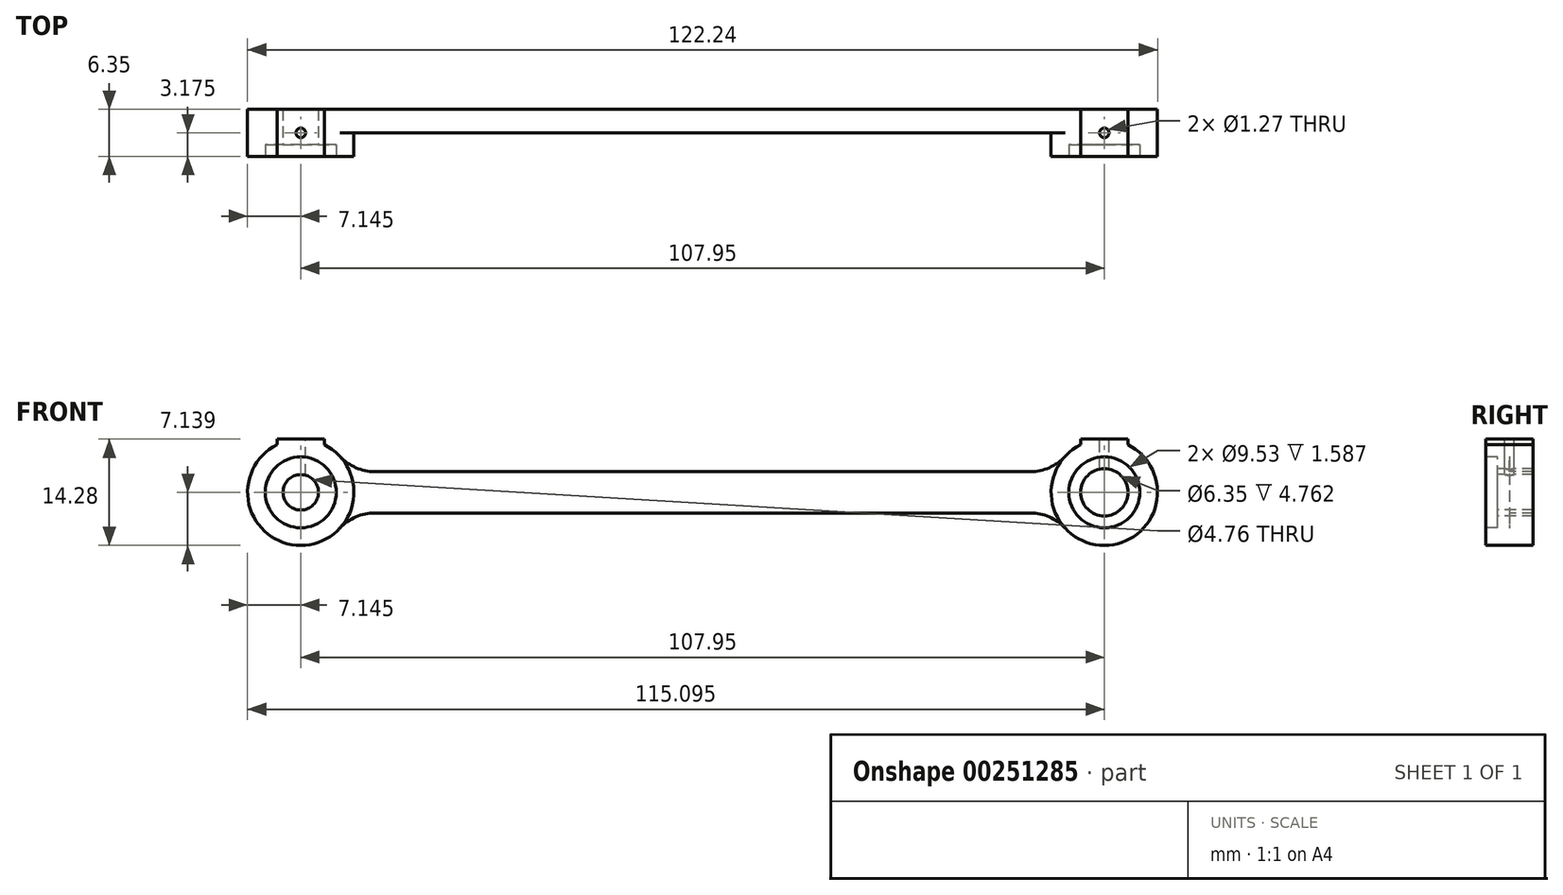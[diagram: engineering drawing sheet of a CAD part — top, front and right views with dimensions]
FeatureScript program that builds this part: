
annotation { "Feature Type Name" : "Feature", "Feature Type Description" : "" }
export const myFeature = defineFeature(function(context is Context, id is Id, definition is map)
    precondition{}
    {
        {
            var Q0;
            Q0=qCreatedBy(makeId("Front.planeOp"),FACE);
            var sketch = newSketch(context, id + "F0", { "sketchPlane" : qUnion([Q0])});
            skLineSegment(sketch, "E0", {"start": v(3.78, 14.91) * mm, "end": v(111.73, 14.91) * mm});
            skLineSegment(sketch, "E1", {"start": v(111.73, 14.91) * mm, "end": v(111.73, 20.47) * mm});
            skLineSegment(sketch, "E2", {"start": v(111.73, 20.47) * mm, "end": v(3.78, 20.47) * mm});
            skLineSegment(sketch, "E3", {"start": v(3.78, 20.47) * mm, "end": v(3.78, 14.91) * mm});
            skSolve(sketch);
        }
        {
            var Q0;
            Q0 = qSketchRegion(id + "F0", true);
            extrude(context, id + "F1", {"entities" : qUnion([Q0]), "depth" : 3.17 * mm});
        }
        {
            var Q0;
            Q0=makeQuery(id+"F1.opExtrude","CAP_FACE",FACE,{"disambiguationData":[OSD([sQuery(id+"F0.wireOp",EDGE,"E0"),sQuery(id+"F0.wireOp",EDGE,"E1"),sQuery(id+"F0.wireOp",EDGE,"E2"),sQuery(id+"F0.wireOp",EDGE,"E3")])],"isStart":false});
            var sketch = newSketch(context, id + "F2", { "sketchPlane" : qUnion([Q0])});
            skCircle(sketch, "E4", {"center": v(3.78, 17.69) * mm, "radius": 7.14 * mm});
            skSolve(sketch);
        }
        {
            var Q0;
            Q0 = qSketchRegion(id + "F2", true);
            extrude(context, id + "F3", {"entities" : qUnion([Q0]), "operationType" : NewBodyOperationType.ADD, "oppositeDirection" : true, "depth" : 3.17 * mm});
        }
        {
            var Q0;
            Q0=makeQuery(id+"F3.boolean.opBoolean","MERGE",FACE,{"derivedFrom":[makeQuery(id+"F1.opExtrude","CAP_FACE",FACE,{"disambiguationData":[OSD([sQuery(id+"F0.wireOp",EDGE,"E0"),sQuery(id+"F0.wireOp",EDGE,"E1"),sQuery(id+"F0.wireOp",EDGE,"E2"),sQuery(id+"F0.wireOp",EDGE,"E3")])],"isStart":false}),makeQuery(id+"F3.opExtrude","CAP_FACE",FACE,{"disambiguationData":[OSD([sQuery(id+"F2.wireOp",EDGE,"E4")])],"isStart":true})]});
            var sketch = newSketch(context, id + "F4", { "sketchPlane" : qUnion([Q0])});
            skCircle(sketch, "E5", {"center": v(3.78, 17.69) * mm, "radius": 7.14 * mm});
            skSolve(sketch);
        }
        {
            var Q0;
            Q0 = qSketchRegion(id + "F4", true);
            extrude(context, id + "F5", {"entities" : qUnion([Q0]), "operationType" : NewBodyOperationType.ADD, "depth" : 3.17 * mm});
        }
        {
            var Q0;
            Q0=makeQuery(id+"F5.opExtrude","CAP_FACE",FACE,{"disambiguationData":[OSD([sQuery(id+"F4.wireOp",EDGE,"E5")])],"isStart":false});
            var sketch = newSketch(context, id + "F6", { "sketchPlane" : qUnion([Q0])});
            skCircle(sketch, "E6", {"center": v(3.78, 17.69) * mm, "radius": 2.38 * mm});
            skSolve(sketch);
        }
        {
            var Q0;
            Q0 = qSketchRegion(id + "F6", true);
            extrude(context, id + "F7", {"entities" : qUnion([Q0]), "operationType" : NewBodyOperationType.REMOVE, "oppositeDirection" : true, "depth" : 25.4 * mm});
        }
        {
            var Q0;
            Q0=makeQuery(id+"F5.opExtrude","CAP_FACE",FACE,{"disambiguationData":[OSD([sQuery(id+"F4.wireOp",EDGE,"E5")])],"isStart":false});
            var sketch = newSketch(context, id + "F8", { "sketchPlane" : qUnion([Q0])});
            skCircle(sketch, "E7", {"center": v(3.78, 17.69) * mm, "radius": 4.76 * mm});
            skSolve(sketch);
        }
        {
            var Q0;
            Q0 = qSketchRegion(id + "F8", true);
            extrude(context, id + "F9", {"entities" : qUnion([Q0]), "operationType" : NewBodyOperationType.REMOVE, "oppositeDirection" : true, "depth" : 1.59 * mm});
        }
        {
            var Q0;
            Q0=makeQuery(id+"F5.opExtrude","CAP_FACE",FACE,{"disambiguationData":[OSD([sQuery(id+"F4.wireOp",EDGE,"E5")])],"isStart":false});
            var sketch = newSketch(context, id + "F10", { "sketchPlane" : qUnion([Q0])});
            skLineSegment(sketch, "E8", {"start": v(-3.24, 24.83) * mm, "end": v(11.05, 24.83) * mm});
            skLineSegment(sketch, "E9", {"start": v(0.6, 24.83) * mm, "end": v(0.6, 24.09) * mm});
            skLineSegment(sketch, "E10", {"start": v(3.78, 17.69) * mm, "end": v(3.78, 24.83) * mm});
            skLineSegment(sketch, "E11", {"start": v(6.96, 24.83) * mm, "end": v(6.96, 24.09) * mm});
            skArc(sketch, "E12", {"start": v(0.6, 24.09) * mm, "mid": v(3.78, 24.83) * mm, "end": v(6.96, 24.09) * mm});
            skSolve(sketch);
        }
        {
            var Q0;
            Q0 = qSketchRegion(id + "F10", true);
            extrude(context, id + "F11", {"entities" : qUnion([Q0]), "oppositeDirection" : true, "depth" : 6.35 * mm});
        }
        {
            var Q0;
            {var subQ0=sQuery(id+"F10.wireOp",EDGE,"E8");Q0=makeQuery(id+"F11.opExtrude","SWEPT_FACE",FACE,{"disambiguationData":[OSD([subQ0]),TDD([makeQuery(id+"F10.imprint","IMPRINT",EDGE,{"disambiguationData":[TD([[makeQuery(id+"F10.imprint","INTERSECT",VERTEX,{"derivedFrom":[subQ0,sQuery(id+"F10.wireOp",EDGE,"E9")]}),-1.0]])],"derivedFrom":subQ0})])]});}
            var sketch = newSketch(context, id + "F12", { "sketchPlane" : qUnion([Q0])});
            skCircle(sketch, "E13", {"center": v(3.78, -3.17) * mm, "radius": 0.64 * mm});
            skSolve(sketch);
        }
        {
            var Q0;
            Q0=makeQuery(id+"F1.opExtrude","SWEPT_BODY",BODY,{"disambiguationData":[OSD([sQuery(id+"F0.wireOp",EDGE,"E0"),sQuery(id+"F0.wireOp",EDGE,"E1"),sQuery(id+"F0.wireOp",EDGE,"E2"),sQuery(id+"F0.wireOp",EDGE,"E3")])]});
            var Q1;
            Q1=makeQuery(id+"F11.opExtrude","SWEPT_BODY",BODY,{"disambiguationData":[OSD([sQuery(id+"F10.wireOp",EDGE,"E8"),sQuery(id+"F10.wireOp",EDGE,"E9"),sQuery(id+"F10.wireOp",EDGE,"E12")])]});
            var Q2;
            Q2=makeQuery(id+"F11.opExtrude","SWEPT_BODY",BODY,{"disambiguationData":[OSD([sQuery(id+"F10.wireOp",EDGE,"E8"),sQuery(id+"F10.wireOp",EDGE,"E11"),sQuery(id+"F10.wireOp",EDGE,"E12")])]});
            booleanBodies(context, id + "F13", {"operationType" : BooleanOperationType.UNION, "tools" : qUnion([Q0, Q1, Q2])});
        }
        {
            var Q0;
            {var subQ0=sQuery(id+"F12.wireOp",EDGE,"E13");var subQ1=sQuery(id+"F10.wireOp",EDGE,"E12");var subQ2=sQuery(id+"F10.wireOp",EDGE,"E8");var subQ3=makeQuery(id+"F11.opExtrude","SWEPT_EDGE",EDGE,{"disambiguationData":[OSD([subQ2,subQ1]),ownerDisambiguation([makeQuery(id+"F11.opExtrude","SWEPT_BODY",BODY,{"disambiguationData":[OSD([subQ2,sQuery(id+"F10.wireOp",EDGE,"E9"),subQ1])]})])]});var subQ4=makeQuery(id+"F12.imprint","INTERSECT",VERTEX,{"disambiguationData":[OD(0.0)],"derivedFrom":[subQ3,subQ0]});Q0=makeQuery(id+"F12.imprint","IMPRINT",FACE,{"disambiguationData":[TD([[makeQuery(id+"F12.imprint","IMPRINT",EDGE,{"disambiguationData":[TD([[subQ4,1.0]])],"derivedFrom":subQ0}),1.0]])]});}
            var Q1;
            {var subQ0=sQuery(id+"F12.wireOp",EDGE,"E13");var subQ1=sQuery(id+"F10.wireOp",EDGE,"E12");var subQ2=sQuery(id+"F10.wireOp",EDGE,"E8");var subQ3=makeQuery(id+"F11.opExtrude","SWEPT_EDGE",EDGE,{"disambiguationData":[OSD([subQ2,subQ1]),ownerDisambiguation([makeQuery(id+"F11.opExtrude","SWEPT_BODY",BODY,{"disambiguationData":[OSD([subQ2,sQuery(id+"F10.wireOp",EDGE,"E9"),subQ1])]})])]});var subQ4=makeQuery(id+"F12.imprint","INTERSECT",VERTEX,{"disambiguationData":[OD(0.0)],"derivedFrom":[subQ3,subQ0]});Q1=makeQuery(id+"F12.imprint","IMPRINT",FACE,{"disambiguationData":[TD([[makeQuery(id+"F12.imprint","IMPRINT",EDGE,{"disambiguationData":[TD([[subQ4,-1.0]])],"derivedFrom":subQ0}),1.0]])]});}
            extrude(context, id + "F14", {"entities" : qUnion([Q0, Q1]), "operationType" : NewBodyOperationType.REMOVE, "oppositeDirection" : true, "depth" : 6.35 * mm});
        }
        {
            var Q0;
            Q0=makeQuery(id+"F3.boolean.opBoolean","MERGE",FACE,{"derivedFrom":[makeQuery(id+"F1.opExtrude","CAP_FACE",FACE,{"disambiguationData":[OSD([sQuery(id+"F0.wireOp",EDGE,"E0"),sQuery(id+"F0.wireOp",EDGE,"E1"),sQuery(id+"F0.wireOp",EDGE,"E2"),sQuery(id+"F0.wireOp",EDGE,"E3")])],"isStart":false}),makeQuery(id+"F3.opExtrude","CAP_FACE",FACE,{"disambiguationData":[OSD([sQuery(id+"F2.wireOp",EDGE,"E4")])],"isStart":true})]});
            var sketch = newSketch(context, id + "F15", { "sketchPlane" : qUnion([Q0])});
            skCircle(sketch, "E14", {"center": v(111.73, 17.69) * mm, "radius": 7.14 * mm});
            skSolve(sketch);
        }
        {
            var Q0;
            Q0 = qSketchRegion(id + "F15", true);
            extrude(context, id + "F16", {"entities" : qUnion([Q0]), "operationType" : NewBodyOperationType.ADD, "oppositeDirection" : true, "depth" : 3.17 * mm});
        }
        {
            var Q0;
            Q0=makeQuery(id+"F16.boolean.opBoolean","MERGE",FACE,{"derivedFrom":[makeQuery(id+"F3.boolean.opBoolean","MERGE",FACE,{"derivedFrom":[makeQuery(id+"F1.opExtrude","CAP_FACE",FACE,{"disambiguationData":[OSD([sQuery(id+"F0.wireOp",EDGE,"E0"),sQuery(id+"F0.wireOp",EDGE,"E1"),sQuery(id+"F0.wireOp",EDGE,"E2"),sQuery(id+"F0.wireOp",EDGE,"E3")])],"isStart":false}),makeQuery(id+"F3.opExtrude","CAP_FACE",FACE,{"disambiguationData":[OSD([sQuery(id+"F2.wireOp",EDGE,"E4")])],"isStart":true})]}),makeQuery(id+"F16.opExtrude","CAP_FACE",FACE,{"disambiguationData":[OSD([sQuery(id+"F15.wireOp",EDGE,"E14")])],"isStart":true})]});
            var sketch = newSketch(context, id + "F17", { "sketchPlane" : qUnion([Q0])});
            skCircle(sketch, "E15", {"center": v(111.73, 17.69) * mm, "radius": 7.14 * mm});
            skSolve(sketch);
        }
        {
            var Q0;
            Q0 = qSketchRegion(id + "F17", true);
            extrude(context, id + "F18", {"entities" : qUnion([Q0]), "operationType" : NewBodyOperationType.ADD, "depth" : 3.17 * mm});
        }
        {
            var Q0;
            Q0=makeQuery(id+"F18.opExtrude","CAP_FACE",FACE,{"disambiguationData":[OSD([sQuery(id+"F17.wireOp",EDGE,"E15")])],"isStart":false});
            var sketch = newSketch(context, id + "F19", { "sketchPlane" : qUnion([Q0])});
            skCircle(sketch, "E16", {"center": v(111.73, 17.69) * mm, "radius": 3.18 * mm});
            skSolve(sketch);
        }
        {
            var Q0;
            Q0 = qSketchRegion(id + "F19", true);
            extrude(context, id + "F20", {"entities" : qUnion([Q0]), "operationType" : NewBodyOperationType.REMOVE, "oppositeDirection" : true, "depth" : 25.4 * mm});
        }
        {
            var Q0;
            Q0=makeQuery(id+"F18.opExtrude","CAP_FACE",FACE,{"disambiguationData":[OSD([sQuery(id+"F17.wireOp",EDGE,"E15")])],"isStart":false});
            var sketch = newSketch(context, id + "F21", { "sketchPlane" : qUnion([Q0])});
            skCircle(sketch, "E17", {"center": v(111.73, 17.69) * mm, "radius": 4.76 * mm});
            skSolve(sketch);
        }
        {
            var Q0;
            Q0 = qSketchRegion(id + "F21", true);
            extrude(context, id + "F22", {"entities" : qUnion([Q0]), "operationType" : NewBodyOperationType.REMOVE, "oppositeDirection" : true, "depth" : 1.59 * mm});
        }
        {
            var Q0;
            Q0=makeQuery(id+"F18.opExtrude","CAP_FACE",FACE,{"disambiguationData":[OSD([sQuery(id+"F17.wireOp",EDGE,"E15")])],"isStart":false});
            var sketch = newSketch(context, id + "F23", { "sketchPlane" : qUnion([Q0])});
            skLineSegment(sketch, "E18", {"start": v(103.62, 24.83) * mm, "end": v(118.22, 24.83) * mm});
            skLineSegment(sketch, "E19", {"start": v(108.56, 24.83) * mm, "end": v(108.56, 24.09) * mm});
            skLineSegment(sketch, "E20", {"start": v(114.9, 24.83) * mm, "end": v(114.9, 24.09) * mm});
            skLineSegment(sketch, "E21", {"start": v(111.73, 17.69) * mm, "end": v(111.73, 24.83) * mm});
            skArc(sketch, "E22", {"start": v(108.56, 24.09) * mm, "mid": v(111.73, 24.83) * mm, "end": v(114.9, 24.09) * mm});
            skSolve(sketch);
        }
        {
            var Q0;
            Q0 = qSketchRegion(id + "F23", true);
            extrude(context, id + "F24", {"entities" : qUnion([Q0]), "operationType" : NewBodyOperationType.ADD, "oppositeDirection" : true, "depth" : 6.35 * mm});
        }
        {
            var Q0;
            {var subQ0=sQuery(id+"F23.wireOp",EDGE,"E18");Q0=makeQuery(id+"F24.boolean.opBoolean","MERGE",FACE,{"derivedFrom":[makeQuery(id+"F24.opExtrude","SWEPT_FACE",FACE,{"disambiguationData":[OSD([subQ0]),TDD([makeQuery(id+"F23.imprint","IMPRINT",EDGE,{"disambiguationData":[TD([[makeQuery(id+"F23.imprint","INTERSECT",VERTEX,{"derivedFrom":[subQ0,sQuery(id+"F23.wireOp",EDGE,"E19")]}),-1.0]])],"derivedFrom":subQ0})])]}),makeQuery(id+"F24.opExtrude","SWEPT_FACE",FACE,{"disambiguationData":[OSD([subQ0]),TDD([makeQuery(id+"F23.imprint","IMPRINT",EDGE,{"disambiguationData":[TD([[makeQuery(id+"F23.imprint","INTERSECT",VERTEX,{"derivedFrom":[subQ0,sQuery(id+"F23.wireOp",EDGE,"E20")]}),1.0]])],"derivedFrom":subQ0})])]})]});}
            var sketch = newSketch(context, id + "F25", { "sketchPlane" : qUnion([Q0])});
            skCircle(sketch, "E23", {"center": v(111.73, -3.18) * mm, "radius": 0.64 * mm});
            skSolve(sketch);
        }
        {
            var Q0;
            Q0 = qSketchRegion(id + "F25", true);
            extrude(context, id + "F26", {"entities" : qUnion([Q0]), "operationType" : NewBodyOperationType.REMOVE, "oppositeDirection" : true, "depth" : 6.35 * mm});
        }
        {
            var Q0;
            Q0=makeQuery(id+"F3.boolean.opBoolean","INTERSECT",EDGE,{"derivedFrom":[makeQuery(id+"F1.opExtrude","SWEPT_FACE",FACE,{"disambiguationData":[OSD([sQuery(id+"F0.wireOp",EDGE,"E2")])]}),makeQuery(id+"F3.opExtrude","SWEPT_FACE",FACE,{"disambiguationData":[OSD([sQuery(id+"F2.wireOp",EDGE,"E4")])]})]});
            var Q1;
            Q1=makeQuery(id+"F3.boolean.opBoolean","INTERSECT",EDGE,{"derivedFrom":[makeQuery(id+"F1.opExtrude","SWEPT_FACE",FACE,{"disambiguationData":[OSD([sQuery(id+"F0.wireOp",EDGE,"E0")])]}),makeQuery(id+"F3.opExtrude","SWEPT_FACE",FACE,{"disambiguationData":[OSD([sQuery(id+"F2.wireOp",EDGE,"E4")])]})]});
            var Q2;
            Q2=makeQuery(id+"F16.boolean.opBoolean","INTERSECT",EDGE,{"derivedFrom":[makeQuery(id+"F1.opExtrude","SWEPT_FACE",FACE,{"disambiguationData":[OSD([sQuery(id+"F0.wireOp",EDGE,"E2")])]}),makeQuery(id+"F16.opExtrude","SWEPT_FACE",FACE,{"disambiguationData":[OSD([sQuery(id+"F15.wireOp",EDGE,"E14")])]})]});
            var Q3;
            Q3=makeQuery(id+"F16.boolean.opBoolean","INTERSECT",EDGE,{"derivedFrom":[makeQuery(id+"F1.opExtrude","SWEPT_FACE",FACE,{"disambiguationData":[OSD([sQuery(id+"F0.wireOp",EDGE,"E0")])]}),makeQuery(id+"F16.opExtrude","SWEPT_FACE",FACE,{"disambiguationData":[OSD([sQuery(id+"F15.wireOp",EDGE,"E14")])]})]});
            var Q4;
            Q4=makeQuery(id+"F11.opExtrude","SWEPT_EDGE",EDGE,{"disambiguationData":[OSD([sQuery(id+"F4.wireOp",EDGE,"E5"),sQuery(id+"F10.wireOp",EDGE,"E11"),sQuery(id+"F10.wireOp",EDGE,"E12")])]});
            var Q5;
            Q5=makeQuery(id+"F11.opExtrude","SWEPT_EDGE",EDGE,{"disambiguationData":[OSD([sQuery(id+"F4.wireOp",EDGE,"E5"),sQuery(id+"F10.wireOp",EDGE,"E9"),sQuery(id+"F10.wireOp",EDGE,"E12")])]});
            var Q6;
            Q6=makeQuery(id+"F24.opExtrude","SWEPT_EDGE",EDGE,{"disambiguationData":[OSD([sQuery(id+"F17.wireOp",EDGE,"E15"),sQuery(id+"F23.wireOp",EDGE,"E19"),sQuery(id+"F23.wireOp",EDGE,"E22")])]});
            var Q7;
            Q7=makeQuery(id+"F24.opExtrude","SWEPT_EDGE",EDGE,{"disambiguationData":[OSD([sQuery(id+"F17.wireOp",EDGE,"E15"),sQuery(id+"F23.wireOp",EDGE,"E20"),sQuery(id+"F23.wireOp",EDGE,"E22")])]});
            fillet(context, id + "F27", {"entities" : qUnion([Q0, Q1, Q2, Q3, Q4, Q5, Q6, Q7]), "radius" : 6.35 * mm, "tangentPropagation" : true, "allowEdgeOverflow" : false});
        }
    });
